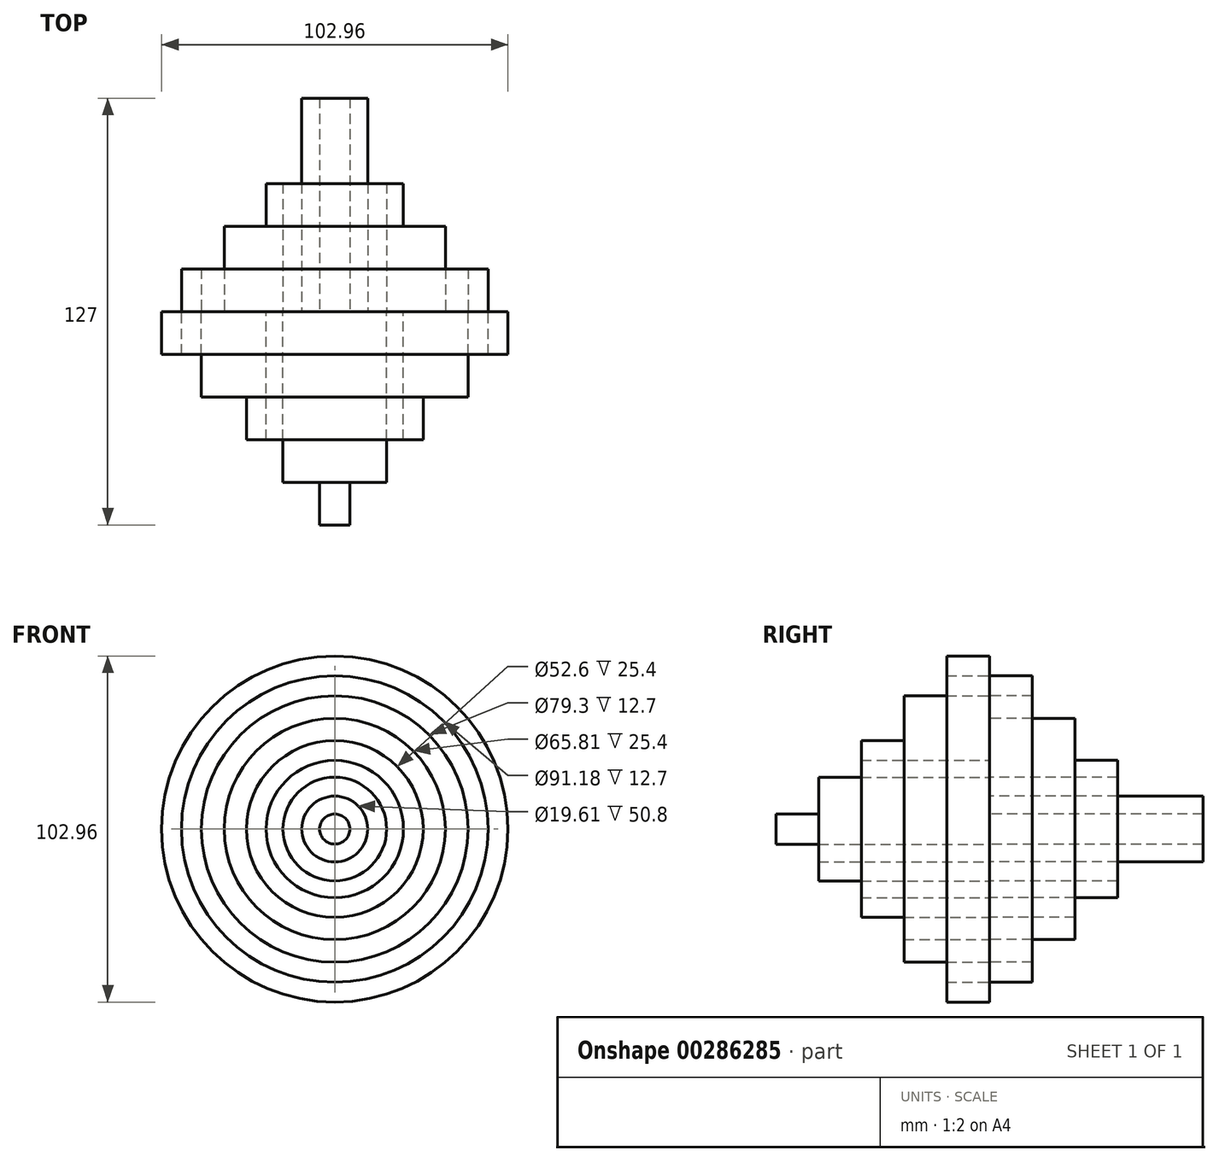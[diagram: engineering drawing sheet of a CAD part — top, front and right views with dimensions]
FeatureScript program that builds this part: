
annotation { "Feature Type Name" : "Feature", "Feature Type Description" : "" }
export const myFeature = defineFeature(function(context is Context, id is Id, definition is map)
    precondition{}
    {
        {
            var Q0;
            Q0=qCreatedBy(makeId("Front.planeOp"),FACE);
            var sketch = newSketch(context, id + "F0", { "sketchPlane" : qUnion([Q0])});
            skCircle(sketch, "E0", {"center": v(0, 0) * mm, "radius": 51.48 * mm});
            skCircle(sketch, "E1", {"center": v(0, 0) * mm, "radius": 39.65 * mm});
            skCircle(sketch, "E2", {"center": v(0, 0) * mm, "radius": 26.3 * mm});
            skCircle(sketch, "E3", {"center": v(0, 0) * mm, "radius": 15.42 * mm});
            skCircle(sketch, "E4", {"center": v(0, 0) * mm, "radius": 45.59 * mm});
            skCircle(sketch, "E5", {"center": v(0, 0) * mm, "radius": 32.9 * mm});
            skCircle(sketch, "E6", {"center": v(0, 0) * mm, "radius": 20.42 * mm});
            skCircle(sketch, "E7", {"center": v(0, 0) * mm, "radius": 9.8 * mm});
            skCircle(sketch, "E8", {"center": v(0, 0) * mm, "radius": 4.48 * mm});
            skSolve(sketch);
        }
        {
            var Q0;
            Q0=makeQuery(id+"F0.imprint","IMPRINT",FACE,{"disambiguationData":[TD([[makeQuery(id+"F0.imprint","IMPRINT",EDGE,{"derivedFrom":sQuery(id+"F0.wireOp",EDGE,"E0")}),1.0]])]});
            extrude(context, id + "F1", {"entities" : qUnion([Q0]), "depth" : 12.7 * mm});
        }
        {
            var Q0;
            Q0=makeQuery(id+"F0.imprint","IMPRINT",FACE,{"disambiguationData":[TD([[makeQuery(id+"F0.imprint","IMPRINT",EDGE,{"derivedFrom":sQuery(id+"F0.wireOp",EDGE,"E1")}),-1.0]])]});
            extrude(context, id + "F2", {"entities" : qUnion([Q0]), "oppositeDirection" : true, "depth" : 12.7 * mm});
        }
        {
            var Q0;
            Q0=makeQuery(id+"F0.imprint","IMPRINT",FACE,{"disambiguationData":[TD([[makeQuery(id+"F0.imprint","IMPRINT",EDGE,{"derivedFrom":sQuery(id+"F0.wireOp",EDGE,"E1")}),1.0]])]});
            extrude(context, id + "F3", {"entities" : qUnion([Q0]), "depth" : 25.4 * mm});
        }
        {
            var Q0;
            Q0=makeQuery(id+"F0.imprint","IMPRINT",FACE,{"disambiguationData":[TD([[makeQuery(id+"F0.imprint","IMPRINT",EDGE,{"derivedFrom":sQuery(id+"F0.wireOp",EDGE,"E2")}),-1.0]])]});
            extrude(context, id + "F4", {"entities" : qUnion([Q0]), "operationType" : NewBodyOperationType.ADD, "oppositeDirection" : true, "depth" : 25.4 * mm});
        }
        {
            var Q0;
            Q0=makeQuery(id+"F0.imprint","IMPRINT",FACE,{"disambiguationData":[TD([[makeQuery(id+"F0.imprint","IMPRINT",EDGE,{"derivedFrom":sQuery(id+"F0.wireOp",EDGE,"E2")}),1.0]])]});
            extrude(context, id + "F5", {"entities" : qUnion([Q0]), "depth" : 38.1 * mm});
        }
        {
            var Q0;
            Q0=makeQuery(id+"F0.imprint","IMPRINT",FACE,{"disambiguationData":[TD([[makeQuery(id+"F0.imprint","IMPRINT",EDGE,{"derivedFrom":sQuery(id+"F0.wireOp",EDGE,"E3")}),-1.0]])]});
            extrude(context, id + "F6", {"entities" : qUnion([Q0]), "operationType" : NewBodyOperationType.ADD, "oppositeDirection" : true, "depth" : 38.1 * mm});
        }
        {
            var Q0;
            Q0=makeQuery(id+"F0.imprint","IMPRINT",FACE,{"disambiguationData":[TD([[makeQuery(id+"F0.imprint","IMPRINT",EDGE,{"derivedFrom":sQuery(id+"F0.wireOp",EDGE,"E3")}),1.0]])]});
            extrude(context, id + "F7", {"entities" : qUnion([Q0]), "depth" : 50.8 * mm});
        }
        {
            var Q0;
            Q0=makeQuery(id+"F0.imprint","IMPRINT",FACE,{"disambiguationData":[TD([[makeQuery(id+"F0.imprint","IMPRINT",EDGE,{"derivedFrom":sQuery(id+"F0.wireOp",EDGE,"E7")}),1.0]])]});
            extrude(context, id + "F8", {"entities" : qUnion([Q0]), "operationType" : NewBodyOperationType.ADD, "oppositeDirection" : true, "depth" : 63.5 * mm});
        }
        {
            var Q0;
            Q0=makeQuery(id+"F0.imprint","IMPRINT",FACE,{"disambiguationData":[TD([[makeQuery(id+"F0.imprint","IMPRINT",EDGE,{"derivedFrom":sQuery(id+"F0.wireOp",EDGE,"E8")}),1.0]])]});
            var Q1;
            Q1=sQuery(id+"F0.wireOp",EDGE,"E8");
            extrude(context, id + "F9", {"entities" : qUnion([Q0]), "surfaceEntities" : qUnion([Q1]), "depth" : 63.5 * mm});
        }
    });
